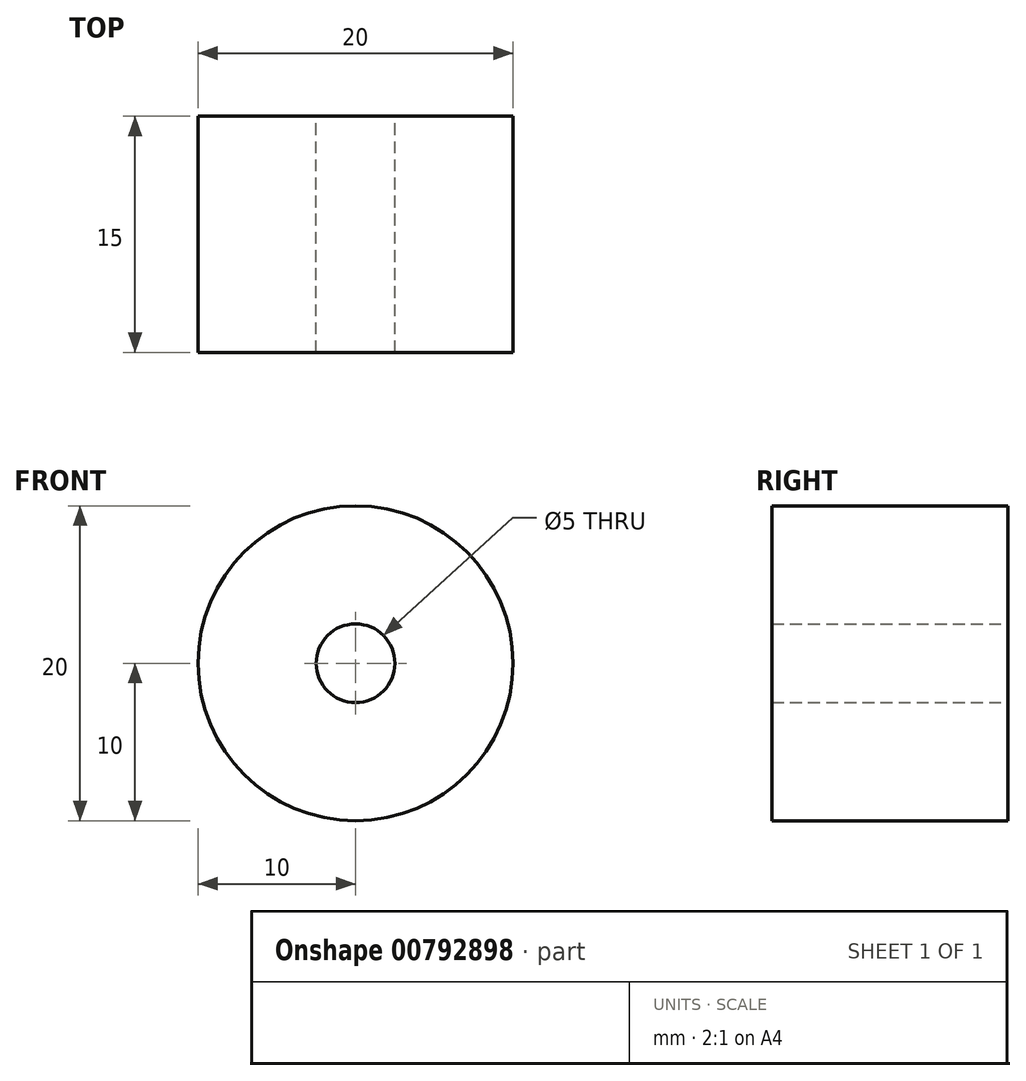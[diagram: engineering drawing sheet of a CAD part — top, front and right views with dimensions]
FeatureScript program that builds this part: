
annotation { "Feature Type Name" : "Feature", "Feature Type Description" : "" }
export const myFeature = defineFeature(function(context is Context, id is Id, definition is map)
    precondition{}
    {
        {
            var Q0;
            Q0=qCreatedBy(makeId("Front.planeOp"),FACE);
            var sketch = newSketch(context, id + "F0", { "sketchPlane" : qUnion([Q0])});
            skCircle(sketch, "E0", {"center": v(0, 0) * mm, "radius": 10 * mm});
            skCircle(sketch, "E1", {"center": v(0, 0) * mm, "radius": 2.5 * mm});
            skSolve(sketch);
        }
        {
            var Q0;
            Q0=makeQuery(id+"F0.imprint","IMPRINT",FACE,{"disambiguationData":[TD([[makeQuery(id+"F0.imprint","IMPRINT",EDGE,{"derivedFrom":sQuery(id+"F0.wireOp",EDGE,"E0")}),1.0]])]});
            extrude(context, id + "F1", {"entities" : qUnion([Q0]), "depth" : 15 * mm, "offsetDistance" : 25 * mm});
        }
    });
